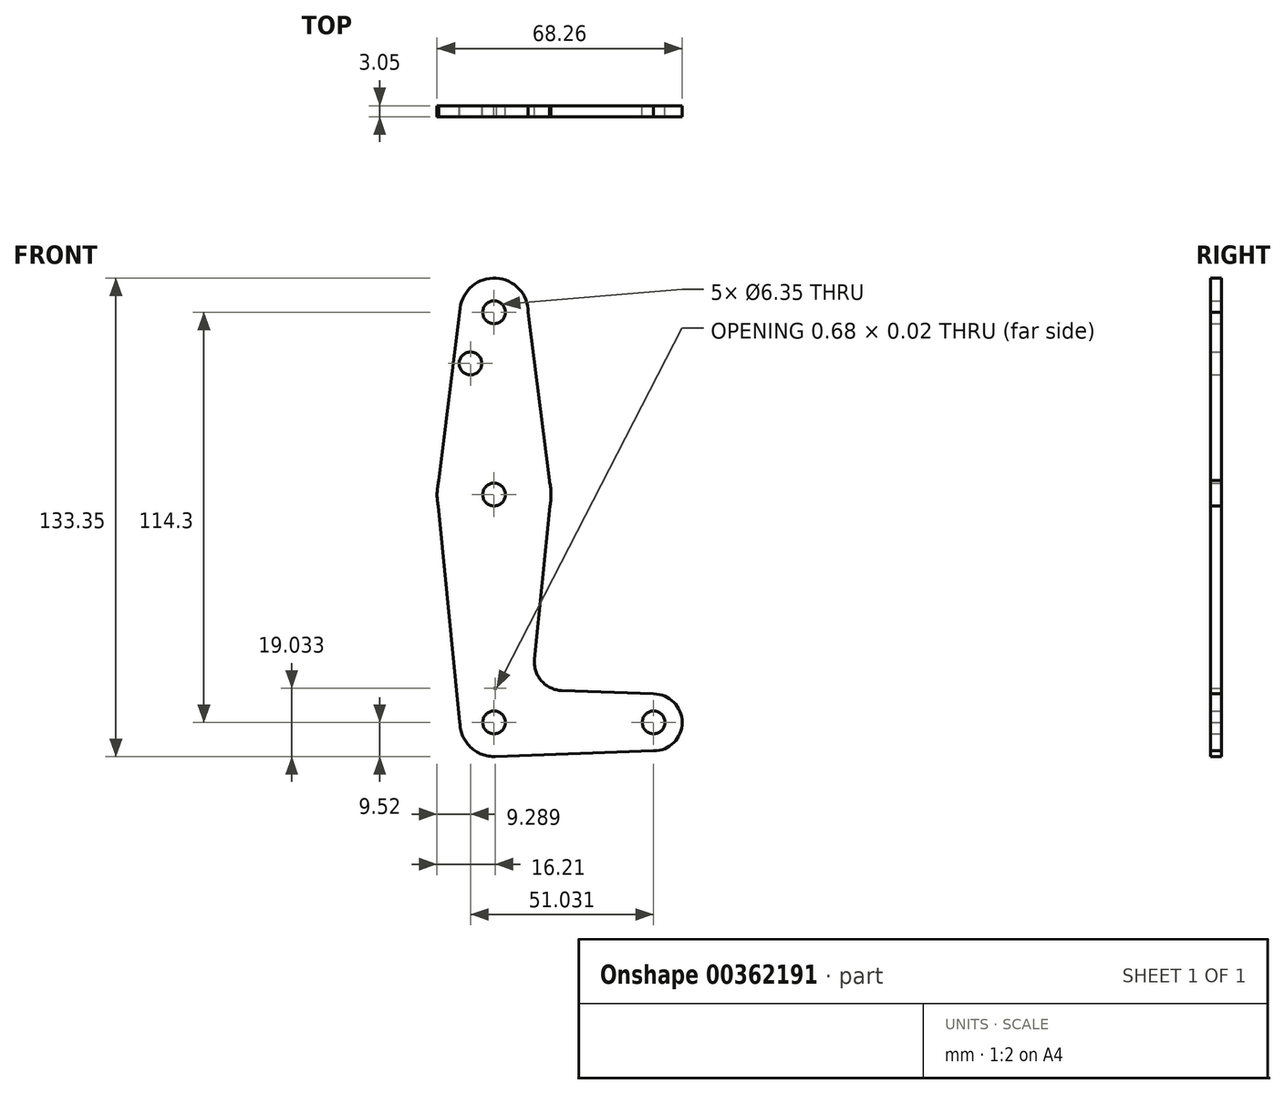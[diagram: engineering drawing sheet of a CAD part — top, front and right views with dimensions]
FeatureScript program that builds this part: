
annotation { "Feature Type Name" : "Feature", "Feature Type Description" : "" }
export const myFeature = defineFeature(function(context is Context, id is Id, definition is map)
    precondition{}
    {
        {
            var Q0;
            Q0=qCreatedBy(makeId("Front.planeOp"),FACE);
            var sketch = newSketch(context, id + "F0", { "sketchPlane" : qUnion([Q0])});
            skLineSegment(sketch, "E0", {"start": v(0, 9.52) * mm, "end": v(0, 63.5) * mm});
            skLineSegment(sketch, "E1", {"start": v(0, 63.5) * mm, "end": v(0, 114.3) * mm});
            skLineSegment(sketch, "E2", {"start": v(9.52, 0) * mm, "end": v(44.45, 0) * mm});
            skCircle(sketch, "E3", {"center": v(0, 114.3) * mm, "radius": 9.53 * mm});
            skCircle(sketch, "E4", {"center": v(0, 63.5) * mm, "radius": 15.88 * mm});
            skCircle(sketch, "E5", {"center": v(0, 0) * mm, "radius": 9.53 * mm});
            skCircle(sketch, "E6", {"center": v(44.45, 0) * mm, "radius": 7.94 * mm});
            skLineSegment(sketch, "E7", {"start": v(15.88, 63.5) * mm, "end": v(9.52, 114.3) * mm});
            skLineSegment(sketch, "E8", {"start": v(-15.88, 63.5) * mm, "end": v(-9.45, 115.47) * mm});
            skLineSegment(sketch, "E9", {"start": v(15.88, 63.5) * mm, "end": v(11.28, 17.59) * mm});
            skLineSegment(sketch, "E10", {"start": v(-15.88, 63.5) * mm, "end": v(-9.52, 0) * mm});
            skLineSegment(sketch, "E11", {"start": v(0, 9.52) * mm, "end": v(0.68, 9.5) * mm});
            skPoint(sketch, "E11.startSnap0", {"position": v(0, 31.75) * mm});
            skLineSegment(sketch, "E12", {"start": v(44.45, -7.94) * mm, "end": v(0, -9.53) * mm});
            skCircle(sketch, "E13", {"center": v(0, 114.3) * mm, "radius": 3.18 * mm});
            skCircle(sketch, "E14", {"center": v(-6.58, 100.03) * mm, "radius": 3.18 * mm});
            skCircle(sketch, "E15", {"center": v(0, 63.5) * mm, "radius": 3.18 * mm});
            skCircle(sketch, "E16", {"center": v(44.45, 0) * mm, "radius": 3.18 * mm});
            skLineSegment(sketch, "E17.trimOffspring", {"start": v(18.91, 8.85) * mm, "end": v(44.45, 7.94) * mm});
            skCircle(sketch, "E18", {"center": v(0, 0) * mm, "radius": 3.18 * mm});
            skPoint(sketch, "E19.visualSharp", {"position": v(10.44, 9.15) * mm});
            skArc(sketch, "E19.filletArc", {"start": v(11.28, 17.59) * mm, "mid": v(13.2, 11.57) * mm, "end": v(18.91, 8.85) * mm});
            skSolve(sketch);
        }
        {
            var Q0;
            Q0 = qSketchRegion(id + "F0", true);
            extrude(context, id + "F1", {"entities" : qUnion([Q0]), "depth" : 3.05 * mm});
        }
    });
